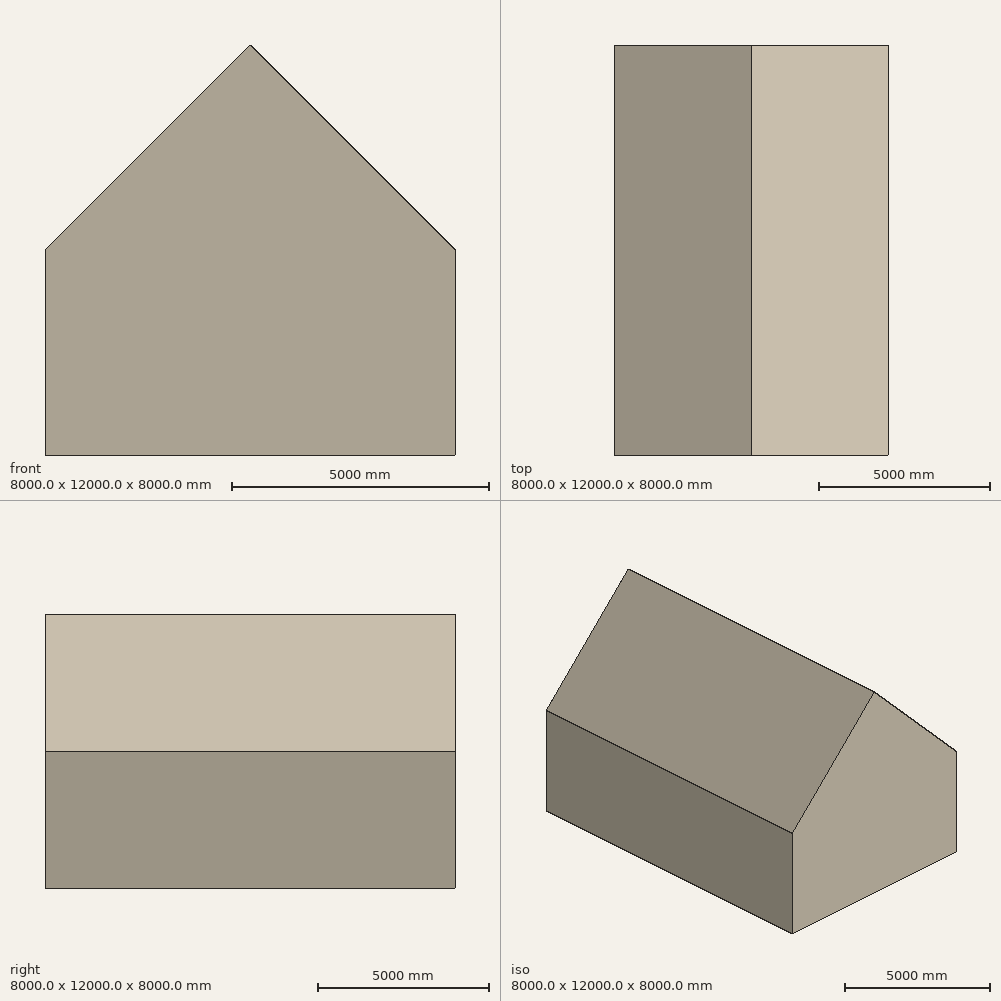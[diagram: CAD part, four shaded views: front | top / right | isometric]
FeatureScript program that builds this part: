
annotation { "Feature Type Name" : "Feature", "Feature Type Description" : "" }
export const myFeature = defineFeature(function(context is Context, id is Id, definition is map)
    precondition{}
    {
        {
            var Q0;
            Q0=qCreatedBy(makeId("Front.planeOp"),FACE);
            var sketch = newSketch(context, id + "F0", { "sketchPlane" : qUnion([Q0])});
            skLineSegment(sketch, "E0.bottom", {"start": v(0, 0) * mm, "end": v(8000, 0) * mm});
            skLineSegment(sketch, "E0.top", {"start": v(0, 4000) * mm, "end": v(8000, 4000) * mm});
            skLineSegment(sketch, "E0.left", {"start": v(0, 0) * mm, "end": v(0, 4000) * mm});
            skLineSegment(sketch, "E0.right", {"start": v(8000, 0) * mm, "end": v(8000, 4000) * mm});
            skLineSegment(sketch, "E1", {"start": v(0, 4000) * mm, "end": v(4000, 8000) * mm});
            skLineSegment(sketch, "E2", {"start": v(4000, 8000) * mm, "end": v(8000, 4000) * mm});
            skSolve(sketch);
        }
        {
            var Q0;
            Q0=makeQuery(id+"F0.imprint","IMPRINT",FACE,{"disambiguationData":[TD([[makeQuery(id+"F0.imprint","IMPRINT",EDGE,{"derivedFrom":sQuery(id+"F0.wireOp",EDGE,"E0.bottom")}),1.0]])]});
            var Q1;
            Q1=makeQuery(id+"F0.imprint","IMPRINT",FACE,{"disambiguationData":[TD([[makeQuery(id+"F0.imprint","IMPRINT",EDGE,{"derivedFrom":sQuery(id+"F0.wireOp",EDGE,"E0.top")}),1.0]])]});
            extrude(context, id + "F1", {"entities" : qUnion([Q0, Q1]), "depth" : 12000 * mm});
        }
    });
